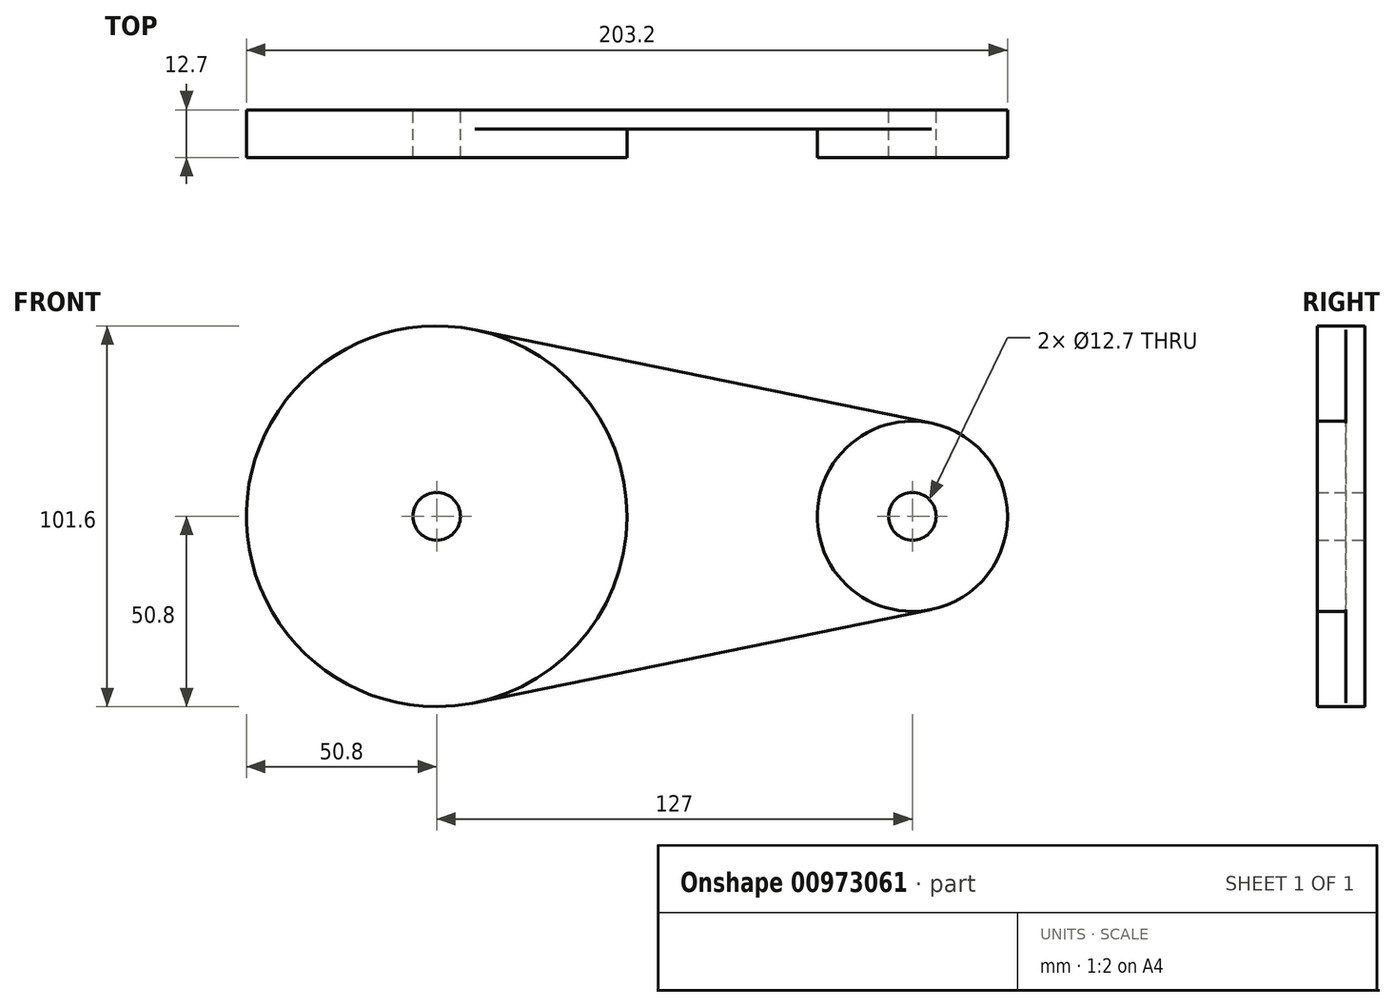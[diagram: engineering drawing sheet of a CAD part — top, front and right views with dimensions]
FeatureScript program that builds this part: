
annotation { "Feature Type Name" : "Feature", "Feature Type Description" : "" }
export const myFeature = defineFeature(function(context is Context, id is Id, definition is map)
    precondition{}
    {
        {
            var Q0;
            Q0=qCreatedBy(makeId("Front.planeOp"),FACE);
            var sketch = newSketch(context, id + "F0", { "sketchPlane" : qUnion([Q0])});
            skCircle(sketch, "E0", {"center": v(0, 0) * mm, "radius": 50.8 * mm});
            skCircle(sketch, "E1", {"center": v(127, 0) * mm, "radius": 25.4 * mm});
            skLineSegment(sketch, "E2", {"start": v(10.16, 49.77) * mm, "end": v(132.08, 24.89) * mm});
            skLineSegment(sketch, "E3", {"start": v(10.16, -49.77) * mm, "end": v(132.08, -24.89) * mm});
            skCircle(sketch, "E4", {"center": v(0, 0) * mm, "radius": 6.35 * mm});
            skCircle(sketch, "E5", {"center": v(127, 0) * mm, "radius": 6.35 * mm});
            skSolve(sketch);
        }
        {
            var Q0;
            {var subQ0=sQuery(id+"F0.wireOp",EDGE,"E1");var subQ1=makeQuery(id+"F0.imprint","INTERSECT",VERTEX,{"derivedFrom":[subQ0,sQuery(id+"F0.wireOp",EDGE,"E2")]});Q0=makeQuery(id+"F0.imprint","IMPRINT",FACE,{"disambiguationData":[TD([[makeQuery(id+"F0.imprint","IMPRINT",EDGE,{"disambiguationData":[TD([[subQ1,-1.0]])],"derivedFrom":subQ0}),1.0]])]});}
            var Q1;
            {var subQ0=sQuery(id+"F0.wireOp",EDGE,"E0");var subQ1=makeQuery(id+"F0.imprint","INTERSECT",VERTEX,{"derivedFrom":[subQ0,sQuery(id+"F0.wireOp",EDGE,"E2")]});Q1=makeQuery(id+"F0.imprint","IMPRINT",FACE,{"disambiguationData":[TD([[makeQuery(id+"F0.imprint","IMPRINT",EDGE,{"disambiguationData":[TD([[subQ1,-1.0]])],"derivedFrom":subQ0}),1.0]])]});}
            extrude(context, id + "F1", {"entities" : qUnion([Q0, Q1]), "depth" : 12.7 * mm, "offsetDistance" : 25.4 * mm});
        }
        {
            var Q0;
            {var subQ0=sQuery(id+"F0.wireOp",EDGE,"E2");Q0=makeQuery(id+"F0.imprint","IMPRINT",FACE,{"disambiguationData":[TD([[makeQuery(id+"F0.imprint","IMPRINT",EDGE,{"derivedFrom":subQ0}),-1.0]])]});}
            extrude(context, id + "F2", {"entities" : qUnion([Q0]), "operationType" : NewBodyOperationType.ADD, "depth" : 5.08 * mm, "offsetDistance" : 25.4 * mm});
        }
        {
            var Q0;
            Q0=makeQuery(id+"F0.imprint","IMPRINT",FACE,{"disambiguationData":[TD([[makeQuery(id+"F0.imprint","IMPRINT",EDGE,{"derivedFrom":sQuery(id+"F0.wireOp",EDGE,"E4")}),1.0]])]});
            extrude(context, id + "F3", {"entities" : qUnion([Q0]), "operationType" : NewBodyOperationType.REMOVE, "depth" : 101.6 * mm, "offsetDistance" : 25.4 * mm});
        }
    });
